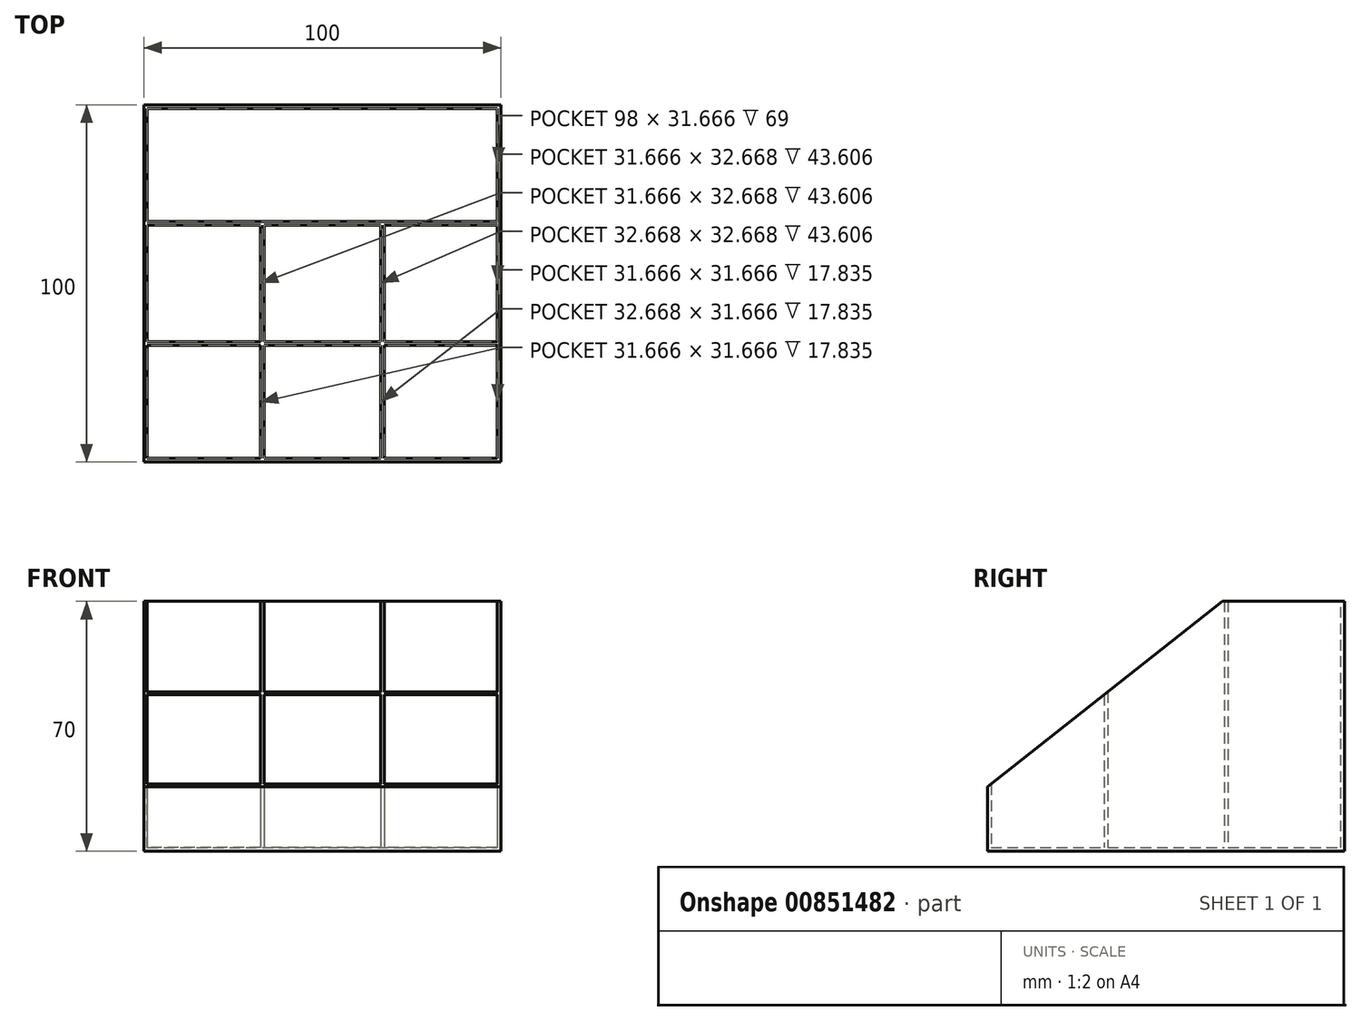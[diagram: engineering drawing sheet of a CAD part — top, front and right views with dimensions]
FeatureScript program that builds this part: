
annotation { "Feature Type Name" : "Feature", "Feature Type Description" : "" }
export const myFeature = defineFeature(function(context is Context, id is Id, definition is map)
    precondition{}
    {
        {
            var Q0;
            Q0=qCreatedBy(makeId("Top.planeOp"),FACE);
            var sketch = newSketch(context, id + "F0", { "sketchPlane" : qUnion([Q0])});
            skLineSegment(sketch, "E0.bottom", {"start": v(-50, 50) * mm, "end": v(50, 50) * mm});
            skLineSegment(sketch, "E0.top", {"start": v(-50, -50) * mm, "end": v(50, -50) * mm});
            skLineSegment(sketch, "E0.left", {"start": v(-50, 50) * mm, "end": v(-50, -50) * mm});
            skLineSegment(sketch, "E0.right", {"start": v(50, 50) * mm, "end": v(50, -50) * mm});
            skPoint(sketch, "E0.middle", {"position": v(0, 0) * mm});
            skSolve(sketch);
        }
        {
            var Q0;
            Q0=makeQuery(id+"F0.imprint","IMPRINT",FACE,{"disambiguationData":[TD([[makeQuery(id+"F0.imprint","IMPRINT",EDGE,{"derivedFrom":sQuery(id+"F0.wireOp",EDGE,"E0.bottom")}),-1.0]])]});
            extrude(context, id + "F1", {"entities" : qUnion([Q0]), "depth" : 70 * mm, "offsetDistance" : 25 * mm});
        }
        {
            var Q0;
            Q0=makeQuery(id+"F1.opExtrude","CAP_FACE",FACE,{"disambiguationData":[OSD([sQuery(id+"F0.wireOp",EDGE,"E0.bottom"),sQuery(id+"F0.wireOp",EDGE,"E0.top"),sQuery(id+"F0.wireOp",EDGE,"E0.left"),sQuery(id+"F0.wireOp",EDGE,"E0.right")])],"isStart":false});
            var sketch = newSketch(context, id + "F2", { "sketchPlane" : qUnion([Q0])});
            skLineSegment(sketch, "E1.0", {"start": v(-49, 49) * mm, "end": v(-49, -49) * mm});
            skLineSegment(sketch, "E1.1", {"start": v(49, 49) * mm, "end": v(-49, 49) * mm});
            skLineSegment(sketch, "E1.2", {"start": v(49, -49) * mm, "end": v(49, 49) * mm});
            skLineSegment(sketch, "E1.3", {"start": v(-49, -49) * mm, "end": v(49, -49) * mm});
            skSolve(sketch);
        }
        {
            var Q0;
            Q0=makeQuery(id+"F2.imprint","IMPRINT",FACE,{"disambiguationData":[TD([[makeQuery(id+"F2.imprint","IMPRINT",EDGE,{"derivedFrom":sQuery(id+"F2.wireOp",EDGE,"E1.0")}),1.0]])]});
            extrude(context, id + "F3", {"entities" : qUnion([Q0]), "operationType" : NewBodyOperationType.REMOVE, "oppositeDirection" : true, "depth" : 69 * mm, "offsetDistance" : 25 * mm});
        }
        {
            var Q0;
            Q0=makeQuery(id+"F3.boolean.opBoolean","COPY",FACE,{"derivedFrom":makeQuery(id+"F3.opExtrude","CAP_FACE",FACE,{"disambiguationData":[OSD([sQuery(id+"F2.wireOp",EDGE,"E1.0"),sQuery(id+"F2.wireOp",EDGE,"E1.1"),sQuery(id+"F2.wireOp",EDGE,"E1.2"),sQuery(id+"F2.wireOp",EDGE,"E1.3")])],"isStart":false})});
            var sketch = newSketch(context, id + "F4", { "sketchPlane" : qUnion([Q0])});
            skLineSegment(sketch, "E2", {"start": v(16.33, -49) * mm, "end": v(16.33, 49) * mm});
            skLineSegment(sketch, "E3", {"start": v(-16.33, -49) * mm, "end": v(-16.33, 49) * mm});
            skLineSegment(sketch, "E4.0", {"start": v(17.33, -49) * mm, "end": v(17.33, 49) * mm});
            skLineSegment(sketch, "E5.0", {"start": v(-17.33, -49) * mm, "end": v(-17.33, 49) * mm});
            skLineSegment(sketch, "E6", {"start": v(49, -16.33) * mm, "end": v(-49, -16.33) * mm});
            skLineSegment(sketch, "E7", {"start": v(-49, 16.33) * mm, "end": v(49, 16.33) * mm});
            skLineSegment(sketch, "E8.0", {"start": v(49, -17.33) * mm, "end": v(-49, -17.33) * mm});
            skLineSegment(sketch, "E9.0", {"start": v(-54, 54) * mm, "end": v(-54, -54) * mm});
            skLineSegment(sketch, "E9.1", {"start": v(54, 54) * mm, "end": v(-54, 54) * mm});
            skLineSegment(sketch, "E9.2", {"start": v(54, -54) * mm, "end": v(54, 54) * mm});
            skLineSegment(sketch, "E9.3", {"start": v(-54, -54) * mm, "end": v(54, -54) * mm});
            skLineSegment(sketch, "E10.0", {"start": v(-49, 17.33) * mm, "end": v(49, 17.33) * mm});
            skSolve(sketch);
        }
        {
            var Q0;
            {var subQ0=sQuery(id+"F4.wireOp",EDGE,"E8.0");var subQ1=sQuery(id+"F4.wireOp",EDGE,"E4.0");var subQ2=makeQuery(id+"F4.imprint","INTERSECT",VERTEX,{"derivedFrom":[subQ1,subQ0]});Q0=makeQuery(id+"F4.imprint","IMPRINT",FACE,{"disambiguationData":[TD([[makeQuery(id+"F4.imprint","IMPRINT",EDGE,{"disambiguationData":[TD([[subQ2,-1.0]])],"derivedFrom":subQ1}),-1.0]])]});}
            var Q1;
            {var subQ0=sQuery(id+"F4.wireOp",EDGE,"E8.0");var subQ1=sQuery(id+"F4.wireOp",EDGE,"E2");var subQ2=makeQuery(id+"F4.imprint","INTERSECT",VERTEX,{"derivedFrom":[subQ1,subQ0]});Q1=makeQuery(id+"F4.imprint","IMPRINT",FACE,{"disambiguationData":[TD([[makeQuery(id+"F4.imprint","IMPRINT",EDGE,{"disambiguationData":[TD([[subQ2,-1.0]])],"derivedFrom":subQ1}),-1.0]])]});}
            var Q2;
            {var subQ0=sQuery(id+"F4.wireOp",EDGE,"E8.0");var subQ1=sQuery(id+"F4.wireOp",EDGE,"E2");var subQ2=makeQuery(id+"F4.imprint","INTERSECT",VERTEX,{"derivedFrom":[subQ1,subQ0]});Q2=makeQuery(id+"F4.imprint","IMPRINT",FACE,{"disambiguationData":[TD([[makeQuery(id+"F4.imprint","IMPRINT",EDGE,{"disambiguationData":[TD([[subQ2,-1.0]])],"derivedFrom":subQ1}),1.0]])]});}
            var Q3;
            {var subQ0=sQuery(id+"F4.wireOp",EDGE,"E8.0");var subQ1=sQuery(id+"F4.wireOp",EDGE,"E3");var subQ2=makeQuery(id+"F4.imprint","INTERSECT",VERTEX,{"derivedFrom":[subQ1,subQ0]});Q3=makeQuery(id+"F4.imprint","IMPRINT",FACE,{"disambiguationData":[TD([[makeQuery(id+"F4.imprint","IMPRINT",EDGE,{"disambiguationData":[TD([[subQ2,-1.0]])],"derivedFrom":subQ1}),1.0]])]});}
            var Q4;
            {var subQ0=sQuery(id+"F4.wireOp",EDGE,"E8.0");var subQ1=sQuery(id+"F4.wireOp",EDGE,"E5.0");var subQ2=makeQuery(id+"F4.imprint","INTERSECT",VERTEX,{"derivedFrom":[subQ1,subQ0]});Q4=makeQuery(id+"F4.imprint","IMPRINT",FACE,{"disambiguationData":[TD([[makeQuery(id+"F4.imprint","IMPRINT",EDGE,{"disambiguationData":[TD([[subQ2,-1.0]])],"derivedFrom":subQ1}),1.0]])]});}
            var Q5;
            {var subQ0=sQuery(id+"F4.wireOp",EDGE,"E6");var subQ1=sQuery(id+"F4.wireOp",EDGE,"E3");var subQ2=makeQuery(id+"F4.imprint","INTERSECT",VERTEX,{"derivedFrom":[subQ1,subQ0]});Q5=makeQuery(id+"F4.imprint","IMPRINT",FACE,{"disambiguationData":[TD([[makeQuery(id+"F4.imprint","IMPRINT",EDGE,{"disambiguationData":[TD([[subQ2,-1.0]])],"derivedFrom":subQ1}),1.0]])]});}
            var Q6;
            {var subQ0=sQuery(id+"F4.wireOp",EDGE,"E6");var subQ1=sQuery(id+"F4.wireOp",EDGE,"E2");var subQ2=makeQuery(id+"F4.imprint","INTERSECT",VERTEX,{"derivedFrom":[subQ1,subQ0]});Q6=makeQuery(id+"F4.imprint","IMPRINT",FACE,{"disambiguationData":[TD([[makeQuery(id+"F4.imprint","IMPRINT",EDGE,{"disambiguationData":[TD([[subQ2,-1.0]])],"derivedFrom":subQ1}),-1.0]])]});}
            var Q7;
            {var subQ0=sQuery(id+"F4.wireOp",EDGE,"E7");var subQ1=sQuery(id+"F4.wireOp",EDGE,"E4.0");var subQ2=makeQuery(id+"F4.imprint","INTERSECT",VERTEX,{"derivedFrom":[subQ1,subQ0]});Q7=makeQuery(id+"F4.imprint","IMPRINT",FACE,{"disambiguationData":[TD([[makeQuery(id+"F4.imprint","IMPRINT",EDGE,{"disambiguationData":[TD([[subQ2,-1.0]])],"derivedFrom":subQ1}),-1.0]])]});}
            var Q8;
            {var subQ0=sQuery(id+"F4.wireOp",EDGE,"E7");var subQ1=sQuery(id+"F4.wireOp",EDGE,"E2");var subQ2=makeQuery(id+"F4.imprint","INTERSECT",VERTEX,{"derivedFrom":[subQ1,subQ0]});Q8=makeQuery(id+"F4.imprint","IMPRINT",FACE,{"disambiguationData":[TD([[makeQuery(id+"F4.imprint","IMPRINT",EDGE,{"disambiguationData":[TD([[subQ2,-1.0]])],"derivedFrom":subQ1}),-1.0]])]});}
            var Q9;
            {var subQ0=sQuery(id+"F4.wireOp",EDGE,"E7");var subQ1=sQuery(id+"F4.wireOp",EDGE,"E2");var subQ2=makeQuery(id+"F4.imprint","INTERSECT",VERTEX,{"derivedFrom":[subQ1,subQ0]});Q9=makeQuery(id+"F4.imprint","IMPRINT",FACE,{"disambiguationData":[TD([[makeQuery(id+"F4.imprint","IMPRINT",EDGE,{"disambiguationData":[TD([[subQ2,-1.0]])],"derivedFrom":subQ1}),1.0]])]});}
            var Q10;
            {var subQ0=sQuery(id+"F4.wireOp",EDGE,"E7");var subQ1=sQuery(id+"F4.wireOp",EDGE,"E3");var subQ2=makeQuery(id+"F4.imprint","INTERSECT",VERTEX,{"derivedFrom":[subQ1,subQ0]});Q10=makeQuery(id+"F4.imprint","IMPRINT",FACE,{"disambiguationData":[TD([[makeQuery(id+"F4.imprint","IMPRINT",EDGE,{"disambiguationData":[TD([[subQ2,-1.0]])],"derivedFrom":subQ1}),1.0]])]});}
            var Q11;
            {var subQ0=sQuery(id+"F4.wireOp",EDGE,"E7");var subQ1=sQuery(id+"F4.wireOp",EDGE,"E5.0");var subQ2=makeQuery(id+"F4.imprint","INTERSECT",VERTEX,{"derivedFrom":[subQ1,subQ0]});Q11=makeQuery(id+"F4.imprint","IMPRINT",FACE,{"disambiguationData":[TD([[makeQuery(id+"F4.imprint","IMPRINT",EDGE,{"disambiguationData":[TD([[subQ2,-1.0]])],"derivedFrom":subQ1}),1.0]])]});}
            var Q12;
            {var subQ0=sQuery(id+"F4.wireOp",EDGE,"E3");var subQ1=makeQuery(id+"F3.boolean.opBoolean","COPY",EDGE,{"derivedFrom":makeQuery(id+"F3.opExtrude","CAP_EDGE",EDGE,{"disambiguationData":[OSD([sQuery(id+"F2.wireOp",EDGE,"E1.1")])],"isStart":false})});var subQ2=makeQuery(id+"F4.imprint","INTERSECT",VERTEX,{"derivedFrom":[subQ1,subQ0]});Q12=makeQuery(id+"F4.imprint","IMPRINT",FACE,{"disambiguationData":[TD([[makeQuery(id+"F4.imprint","IMPRINT",EDGE,{"disambiguationData":[TD([[subQ2,1.0]])],"derivedFrom":subQ0}),1.0]])]});}
            var Q13;
            {var subQ0=sQuery(id+"F4.wireOp",EDGE,"E2");var subQ1=makeQuery(id+"F3.boolean.opBoolean","COPY",EDGE,{"derivedFrom":makeQuery(id+"F3.opExtrude","CAP_EDGE",EDGE,{"disambiguationData":[OSD([sQuery(id+"F2.wireOp",EDGE,"E1.1")])],"isStart":false})});var subQ2=makeQuery(id+"F4.imprint","INTERSECT",VERTEX,{"derivedFrom":[subQ1,subQ0]});Q13=makeQuery(id+"F4.imprint","IMPRINT",FACE,{"disambiguationData":[TD([[makeQuery(id+"F4.imprint","IMPRINT",EDGE,{"disambiguationData":[TD([[subQ2,1.0]])],"derivedFrom":subQ0}),-1.0]])]});}
            extrude(context, id + "F5", {"entities" : qUnion([Q0, Q1, Q2, Q3, Q4, Q5, Q6, Q7, Q8, Q9, Q10, Q11, Q12, Q13]), "operationType" : NewBodyOperationType.ADD, "depth" : 69 * mm, "offsetDistance" : 25 * mm});
        }
        {
            var Q0;
            Q0=makeQuery(id+"F1.opExtrude","SWEPT_FACE",FACE,{"disambiguationData":[OSD([sQuery(id+"F0.wireOp",EDGE,"E0.left")])]});
            var sketch = newSketch(context, id + "F6", { "sketchPlane" : qUnion([Q0])});
            skLineSegment(sketch, "E11", {"start": v(15.85, 70) * mm, "end": v(-50, 18.05) * mm});
            skSolve(sketch);
        }
        {
            var Q0;
            {var subQ0=sQuery(id+"F6.wireOp",EDGE,"E11");Q0=makeQuery(id+"F6.imprint","IMPRINT",FACE,{"disambiguationData":[TD([[makeQuery(id+"F6.imprint","IMPRINT",EDGE,{"derivedFrom":subQ0}),-1.0]])]});}
            extrude(context, id + "F7", {"entities" : qUnion([Q0]), "operationType" : NewBodyOperationType.REMOVE, "endBound" : BoundingType.THROUGH_ALL, "oppositeDirection" : true, "depth" : 25 * mm, "offsetDistance" : 25 * mm});
        }
        {
            var Q0;
            Q0=makeQuery(id+"F1.opExtrude","SWEPT_BODY",BODY,{"disambiguationData":[OSD([sQuery(id+"F0.wireOp",EDGE,"E0.bottom"),sQuery(id+"F0.wireOp",EDGE,"E0.top"),sQuery(id+"F0.wireOp",EDGE,"E0.left"),sQuery(id+"F0.wireOp",EDGE,"E0.right")])]});
            var Q1;
            Q1=makeQuery(id+"F5.opExtrude","SWEPT_EDGE",EDGE,{"disambiguationData":[OSD([sQuery(id+"F4.wireOp",EDGE,"E2"),sQuery(id+"F4.wireOp",EDGE,"E7")])]});
            transform(context, id + "F8", {"entities" : qUnion([Q0]), "transformType" : TransformType.ROTATION, "transformAxis" : qUnion([Q1]), "angle" : 180 * degree, "makeCopy" : false});
        }
    });
